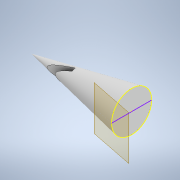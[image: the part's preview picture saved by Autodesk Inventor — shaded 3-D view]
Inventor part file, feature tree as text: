
AUTODESK INVENTOR PART (.ipt)
format: ipt  version: 2021 (Build 250183000, 183)  size: 124,928 bytes
history: native  units: in
note: dims shown in document units (in); Inventor stores cm internally (conversion verified against a paired STEP export)
features: sketch x3, projected_geometry x2, revolve x1, plane x1, extrude x1
ambient origin geometry x8: Origin, YZ Plane, XZ Plane, XY Plane, X Axis, Y Axis, Z Axis, Center Point
bodies: Solid1 (feature_tree)
feature tree (8):
  revolve  "Revolution1"  [1 undecoded]
  sketch  "Sketch2"  dims[d2=90.0deg d3=0.3937in]
  plane  "Work Plane1"
  extrude  "Extrusion1"  Depth=0.3937in
  sketch  "Sketch1"  dims[d0=0.3937in d1=1.9685in]
  projected_geometry  "Projected Loop1"
  sketch  "Sketch3"  dims[d4=0.4724in d6=0.0787in d7=0.3937in d8=0.0in]
  projected_geometry  "Projected Loop2"
note: 1 required parameter value undecoded (feature->parameter linkage not recoverable at this tier; creation-order binding heuristic only, values carry confidence <= 0.55)
